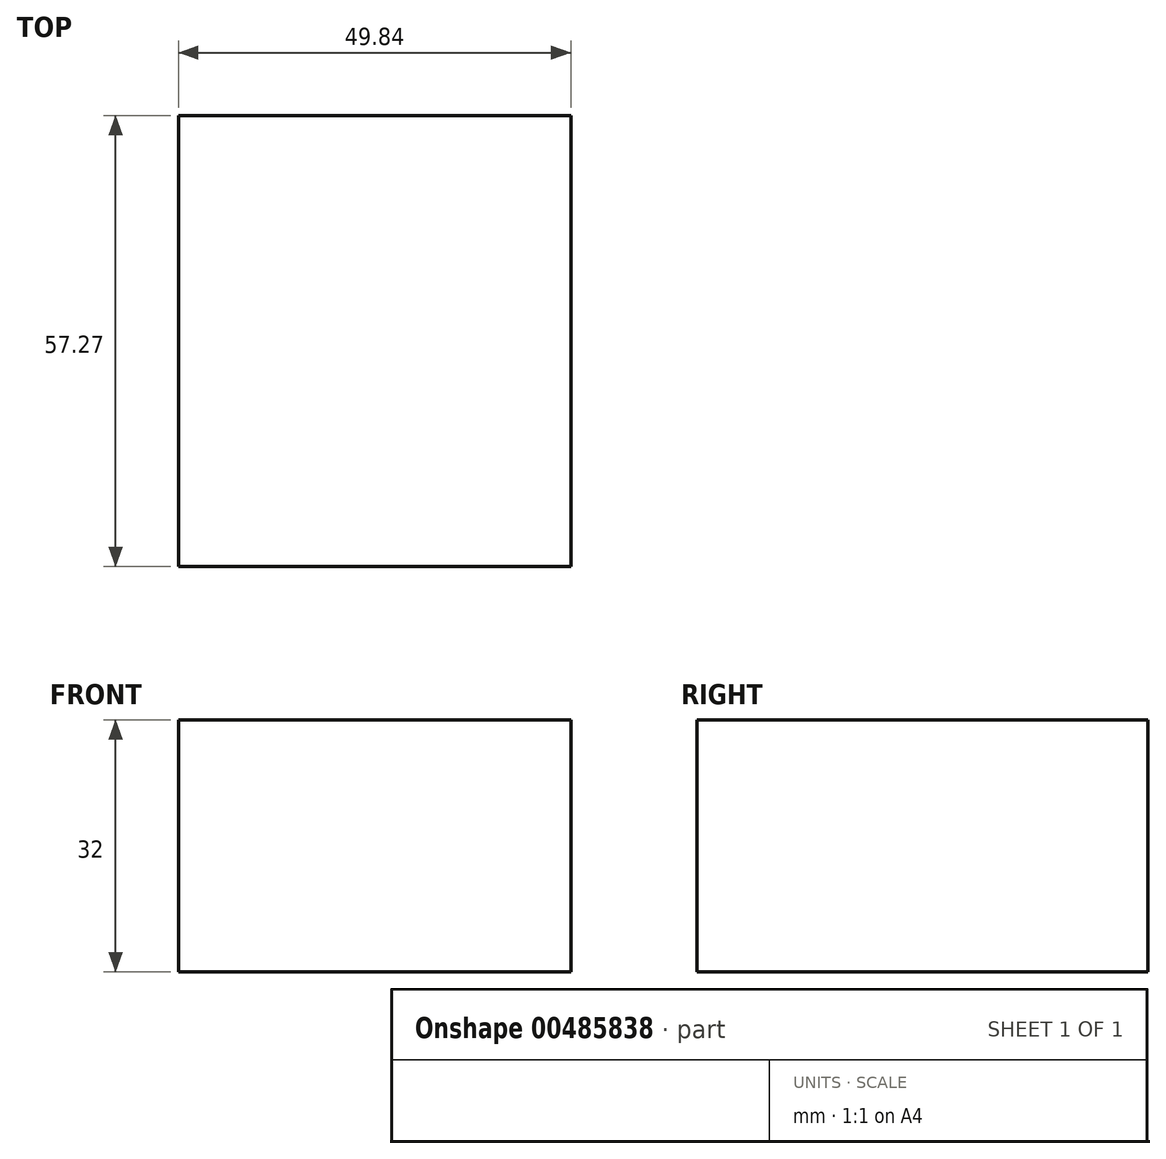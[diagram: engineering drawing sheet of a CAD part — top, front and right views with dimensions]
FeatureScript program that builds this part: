
annotation { "Feature Type Name" : "Feature", "Feature Type Description" : "" }
export const myFeature = defineFeature(function(context is Context, id is Id, definition is map)
    precondition{}
    {
        {
            var Q0;
            Q0=qCreatedBy(makeId("Top.planeOp"),FACE);
            var sketch = newSketch(context, id + "F0", { "sketchPlane" : qUnion([Q0])});
            skLineSegment(sketch, "E0.bottom", {"start": v(-49.84, 57.27) * mm, "end": v(0, 57.27) * mm});
            skLineSegment(sketch, "E0.top", {"start": v(-49.84, 0) * mm, "end": v(0, 0) * mm});
            skLineSegment(sketch, "E0.left", {"start": v(-49.84, 57.27) * mm, "end": v(-49.84, 0) * mm});
            skLineSegment(sketch, "E0.right", {"start": v(0, 57.27) * mm, "end": v(0, 0) * mm});
            skSolve(sketch);
        }
        {
            var Q0;
            Q0 = qSketchRegion(id + "F0", true);
            extrude(context, id + "F1", {"entities" : qUnion([Q0]), "oppositeDirection" : true, "depth" : 32 * mm});
        }
    });
